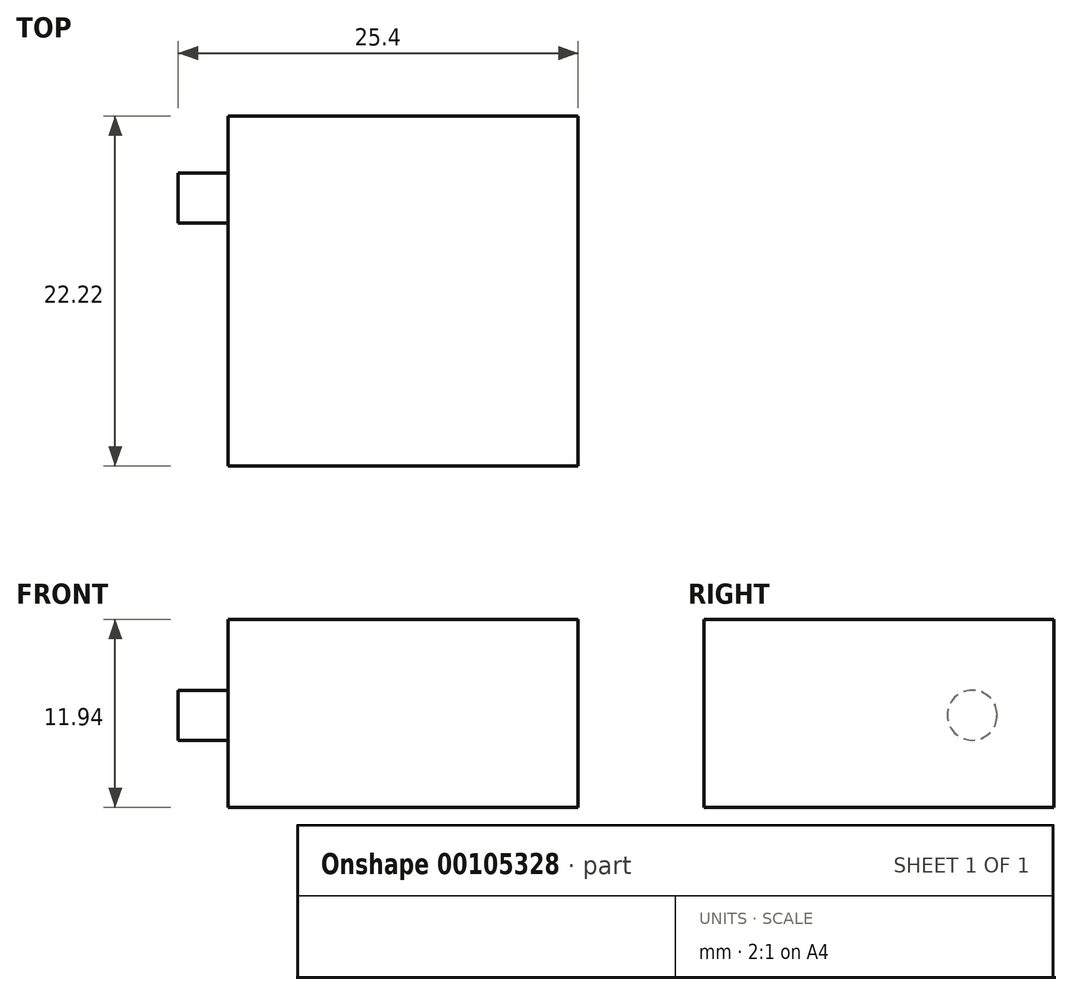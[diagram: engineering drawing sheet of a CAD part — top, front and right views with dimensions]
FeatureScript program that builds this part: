
annotation { "Feature Type Name" : "Feature", "Feature Type Description" : "" }
export const myFeature = defineFeature(function(context is Context, id is Id, definition is map)
    precondition{}
    {
        {
            var Q0;
            Q0=qCreatedBy(makeId("Top.planeOp"),FACE);
            var sketch = newSketch(context, id + "F0", { "sketchPlane" : qUnion([Q0])});
            skLineSegment(sketch, "E0.bottom", {"start": v(-21.48, 28.83) * mm, "end": v(0.74, 28.83) * mm});
            skLineSegment(sketch, "E0.top", {"start": v(-21.48, 6.6) * mm, "end": v(0.74, 6.6) * mm});
            skLineSegment(sketch, "E0.left", {"start": v(-21.48, 28.83) * mm, "end": v(-21.48, 6.6) * mm});
            skLineSegment(sketch, "E0.right", {"start": v(0.74, 28.83) * mm, "end": v(0.74, 6.6) * mm});
            skSolve(sketch);
        }
        {
            var Q0;
            Q0 = qSketchRegion(id + "F0", true);
            var Q1;
            Q1=makeQuery(id+"F0.imprint","IMPRINT",FACE,{"disambiguationData":[TD([[makeQuery(id+"F0.imprint","IMPRINT",EDGE,{"derivedFrom":sQuery(id+"F0.wireOp",EDGE,"E0.bottom")}),-1.0]])]});
            extrude(context, id + "F1", {"entities" : qUnion([Q0, Q1]), "depth" : 11.94 * mm});
        }
        {
            var Q0;
            Q0=makeQuery(id+"F1.opExtrude","SWEPT_FACE",FACE,{"disambiguationData":[OSD([sQuery(id+"F0.wireOp",EDGE,"E0.left")])]});
            var sketch = newSketch(context, id + "F2", { "sketchPlane" : qUnion([Q0])});
            skCircle(sketch, "E1", {"center": v(-23.64, 5.86) * mm, "radius": 1.59 * mm});
            skSolve(sketch);
        }
        {
            var Q0;
            Q0=makeQuery(id+"F2.imprint","IMPRINT",FACE,{"disambiguationData":[TD([[makeQuery(id+"F2.imprint","IMPRINT",EDGE,{"derivedFrom":sQuery(id+"F2.wireOp",EDGE,"E1")}),1.0]])]});
            extrude(context, id + "F3", {"entities" : qUnion([Q0]), "operationType" : NewBodyOperationType.ADD, "depth" : 3.17 * mm});
        }
    });
